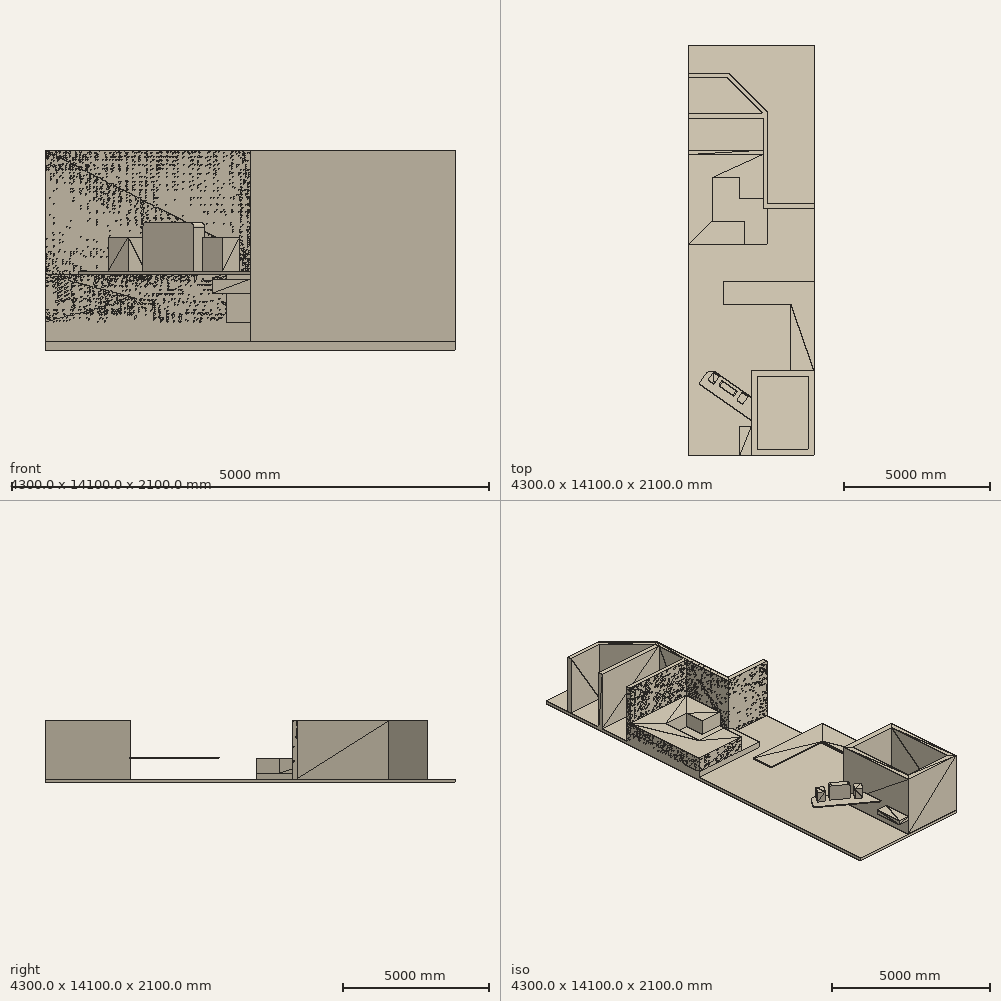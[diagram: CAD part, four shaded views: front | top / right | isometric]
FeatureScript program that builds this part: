
annotation { "Feature Type Name" : "Feature", "Feature Type Description" : "" }
export const myFeature = defineFeature(function(context is Context, id is Id, definition is map)
    precondition{}
    {
        {
            var Q0;
            Q0=qCreatedBy(makeId("Top.planeOp"),FACE);
            var sketch = newSketch(context, id + "F0", { "sketchPlane" : qUnion([Q0])});
            skLineSegment(sketch, "E0.bottom", {"start": v(0, 0) * mm, "end": v(4300, 0) * mm});
            skLineSegment(sketch, "E0.top", {"start": v(0, 14100) * mm, "end": v(4300, 14100) * mm});
            skLineSegment(sketch, "E0.left", {"start": v(0, 0) * mm, "end": v(0, 14100) * mm});
            skLineSegment(sketch, "E0.right", {"start": v(4300, 0) * mm, "end": v(4300, 14100) * mm});
            skLineSegment(sketch, "E1.bottom", {"start": v(-500, -500) * mm, "end": v(4800, -500) * mm});
            skLineSegment(sketch, "E1.top", {"start": v(-500, 14600) * mm, "end": v(4800, 14600) * mm});
            skLineSegment(sketch, "E1.left", {"start": v(-500, -500) * mm, "end": v(-500, 14600) * mm});
            skLineSegment(sketch, "E1.right", {"start": v(4800, -500) * mm, "end": v(4800, 14600) * mm});
            skLineSegment(sketch, "E2", {"start": v(0, 0) * mm, "end": v(-500, -500) * mm});
            skLineSegment(sketch, "E3", {"start": v(4300, 0) * mm, "end": v(4800, -500) * mm});
            skLineSegment(sketch, "E4", {"start": v(-500, 14600) * mm, "end": v(0, 14100) * mm});
            skLineSegment(sketch, "E5", {"start": v(4300, 14100) * mm, "end": v(4800, 14600) * mm});
            skSolve(sketch);
        }
        {
            var Q0;
            Q0=qCreatedBy(makeId("Top.planeOp"),FACE);
            var sketch = newSketch(context, id + "F1", { "sketchPlane" : qUnion([Q0])});
            skLineSegment(sketch, "E6.bottom", {"start": v(2350, 210) * mm, "end": v(4100, 210) * mm});
            skLineSegment(sketch, "E6.top", {"start": v(2350, 2710) * mm, "end": v(4100, 2710) * mm});
            skLineSegment(sketch, "E6.left", {"start": v(2350, 210) * mm, "end": v(2350, 2710) * mm});
            skLineSegment(sketch, "E6.right", {"start": v(4100, 210) * mm, "end": v(4100, 2710) * mm});
            skLineSegment(sketch, "E7.top", {"start": v(2150, 2910) * mm, "end": v(4300, 2910) * mm});
            skLineSegment(sketch, "E7.right", {"start": v(4300, 10) * mm, "end": v(4300, 2910) * mm});
            skLineSegment(sketch, "E8", {"start": v(2150, 2910) * mm, "end": v(2150, 10) * mm});
            skLineSegment(sketch, "E9", {"start": v(2150, 10) * mm, "end": v(4300, 10) * mm});
            skSolve(sketch);
        }
        {
            var Q0;
            Q0=qCreatedBy(makeId("Top.planeOp"),FACE);
            var sketch = newSketch(context, id + "F2", { "sketchPlane" : qUnion([Q0])});
            skLineSegment(sketch, "E10.bottom", {"start": v(346.87, 2461.87) * mm, "end": v(2149, 1200) * mm});
            skLineSegment(sketch, "E10.top", {"start": v(927.53, 2855.28) * mm, "end": v(2149, 2000) * mm});
            skLineSegment(sketch, "E10.right", {"start": v(2149, 1200) * mm, "end": v(2149, 2000) * mm});
            skLineSegment(sketch, "E11.bottom", {"start": v(4300, 2900) * mm, "end": v(3500, 2900) * mm});
            skLineSegment(sketch, "E11.top", {"start": v(4300, 6000) * mm, "end": v(3500, 6000) * mm});
            skLineSegment(sketch, "E11.left", {"start": v(4300, 2900) * mm, "end": v(4300, 6000) * mm});
            skLineSegment(sketch, "E11.right", {"start": v(3500, 2900) * mm, "end": v(3500, 6000) * mm});
            skLineSegment(sketch, "E12.bottom", {"start": v(3500, 6000) * mm, "end": v(1200, 6000) * mm});
            skLineSegment(sketch, "E12.top", {"start": v(3500, 5200) * mm, "end": v(1200, 5200) * mm});
            skLineSegment(sketch, "E12.left", {"start": v(3500, 6000) * mm, "end": v(3500, 5200) * mm});
            skLineSegment(sketch, "E12.right", {"start": v(1200, 6000) * mm, "end": v(1200, 5200) * mm});
            skLineSegment(sketch, "E13", {"start": v(579.35, 2793.89) * mm, "end": v(346.87, 2461.87) * mm});
            skPoint(sketch, "E14.visualSharp", {"position": v(2149, 1200) * mm});
            skPoint(sketch, "E15.visualSharp", {"position": v(722.74, 2998.68) * mm});
            skArc(sketch, "E15.filletArc", {"start": v(927.53, 2855.28) * mm, "mid": v(740.72, 2896.7) * mm, "end": v(579.35, 2793.89) * mm});
            skLineSegment(sketch, "E16.bottom", {"start": v(2149, 1) * mm, "end": v(1749, 1) * mm});
            skLineSegment(sketch, "E16.top", {"start": v(2149, 1001) * mm, "end": v(1749, 1001) * mm});
            skLineSegment(sketch, "E16.left", {"start": v(2149, 1) * mm, "end": v(2149, 1001) * mm});
            skLineSegment(sketch, "E16.right", {"start": v(1749, 1) * mm, "end": v(1749, 1001) * mm});
            skSolve(sketch);
        }
        {
            var Q0;
            Q0=qCreatedBy(makeId("Top.planeOp"),FACE);
            var sketch = newSketch(context, id + "F3", { "sketchPlane" : qUnion([Q0])});
            skLineSegment(sketch, "E17.bottom", {"start": v(0, 7250) * mm, "end": v(2700, 7250) * mm});
            skLineSegment(sketch, "E17.top", {"start": v(0, 10350) * mm, "end": v(2700, 10350) * mm});
            skLineSegment(sketch, "E17.left", {"start": v(0, 7250) * mm, "end": v(0, 10350) * mm});
            skLineSegment(sketch, "E17.right", {"start": v(2700, 7250) * mm, "end": v(2700, 10350) * mm});
            skLineSegment(sketch, "E18.bottom", {"start": v(0, 10350) * mm, "end": v(3100, 10350) * mm});
            skLineSegment(sketch, "E18.top", {"start": v(0, 6850) * mm, "end": v(3100, 6850) * mm});
            skLineSegment(sketch, "E18.left", {"start": v(0, 10350) * mm, "end": v(0, 6850) * mm});
            skLineSegment(sketch, "E18.right", {"start": v(3100, 10350) * mm, "end": v(3100, 6850) * mm});
            skSolve(sketch);
        }
        {
            var Q0;
            Q0=qCreatedBy(makeId("Top.planeOp"),FACE);
            var sketch = newSketch(context, id + "F4", { "sketchPlane" : qUnion([Q0])});
            skLineSegment(sketch, "E19", {"start": v(0, 7250) * mm, "end": v(1900, 7250) * mm});
            skLineSegment(sketch, "E20", {"start": v(1900, 7250) * mm, "end": v(1900, 8050) * mm});
            skLineSegment(sketch, "E21", {"start": v(1900, 8050) * mm, "end": v(800, 8050) * mm});
            skLineSegment(sketch, "E22", {"start": v(800, 8050) * mm, "end": v(800, 9550) * mm});
            skLineSegment(sketch, "E23", {"start": v(800, 9550) * mm, "end": v(1750, 9550) * mm});
            skLineSegment(sketch, "E24", {"start": v(1750, 9550) * mm, "end": v(1750, 8850) * mm});
            skLineSegment(sketch, "E25", {"start": v(1750, 8850) * mm, "end": v(2550, 8850) * mm});
            skLineSegment(sketch, "E26", {"start": v(2550, 8850) * mm, "end": v(2550, 10350) * mm});
            skLineSegment(sketch, "E27", {"start": v(2550, 10350) * mm, "end": v(0, 10350) * mm});
            skLineSegment(sketch, "E28", {"start": v(0, 10350) * mm, "end": v(0, 7250) * mm});
            skSolve(sketch);
        }
        {
            var Q0;
            Q0=qCreatedBy(makeId("Top.planeOp"),FACE);
            var sketch = newSketch(context, id + "F5", { "sketchPlane" : qUnion([Q0])});
            skLineSegment(sketch, "E29", {"start": v(4300, 8500) * mm, "end": v(2550, 8500) * mm});
            skLineSegment(sketch, "E30", {"start": v(2550, 8500) * mm, "end": v(2550, 11750) * mm});
            skLineSegment(sketch, "E31", {"start": v(2550, 11750) * mm, "end": v(1300, 13000) * mm});
            skLineSegment(sketch, "E32", {"start": v(1300, 13000) * mm, "end": v(0, 13000) * mm});
            skLineSegment(sketch, "E33", {"start": v(4300, 8500) * mm, "end": v(4300, 8650) * mm});
            skLineSegment(sketch, "E34", {"start": v(4300, 8650) * mm, "end": v(2700, 8650) * mm});
            skLineSegment(sketch, "E35", {"start": v(2700, 8650) * mm, "end": v(2700, 11812.13) * mm});
            skLineSegment(sketch, "E36", {"start": v(2700, 11812.13) * mm, "end": v(1362.13, 13150) * mm});
            skLineSegment(sketch, "E37", {"start": v(1362.13, 13150) * mm, "end": v(0, 13150) * mm});
            skLineSegment(sketch, "E38", {"start": v(0, 13150) * mm, "end": v(0, 13000) * mm});
            skLineSegment(sketch, "E39.bottom", {"start": v(2550, 10350) * mm, "end": v(0, 10350) * mm});
            skLineSegment(sketch, "E39.top", {"start": v(2550, 10500) * mm, "end": v(0, 10500) * mm});
            skLineSegment(sketch, "E39.left", {"start": v(2550, 10350) * mm, "end": v(2550, 10500) * mm});
            skLineSegment(sketch, "E39.right", {"start": v(0, 10350) * mm, "end": v(0, 10500) * mm});
            skLineSegment(sketch, "E40.bottom", {"start": v(2550, 11750) * mm, "end": v(0, 11750) * mm});
            skLineSegment(sketch, "E40.top", {"start": v(2550, 11600) * mm, "end": v(0, 11600) * mm});
            skLineSegment(sketch, "E40.left", {"start": v(2550, 11750) * mm, "end": v(2550, 11600) * mm});
            skLineSegment(sketch, "E40.right", {"start": v(0, 11750) * mm, "end": v(0, 11600) * mm});
            skSolve(sketch);
        }
        {
            var Q0;
            Q0=makeQuery(id+"F0.imprint","IMPRINT",FACE,{"disambiguationData":[TD([[makeQuery(id+"F0.imprint","IMPRINT",EDGE,{"derivedFrom":sQuery(id+"F0.wireOp",EDGE,"E0.bottom")}),1.0]])]});
            var sketch = newSketch(context, id + "F6", { "sketchPlane" : qUnion([Q0])});
            skLineSegment(sketch, "E41", {"start": v(842.44, 2853.82) * mm, "end": v(657.75, 2590.05) * mm});
            skLineSegment(sketch, "E42", {"start": v(657.75, 2590.05) * mm, "end": v(866.64, 2443.8) * mm});
            skLineSegment(sketch, "E43", {"start": v(866.64, 2443.8) * mm, "end": v(1051.33, 2707.56) * mm});
            skLineSegment(sketch, "E44", {"start": v(1051.33, 2707.56) * mm, "end": v(842.44, 2853.82) * mm});
            skLineSegment(sketch, "E45", {"start": v(1829.52, 2162.66) * mm, "end": v(1644.83, 1898.9) * mm});
            skLineSegment(sketch, "E46", {"start": v(1644.83, 1898.9) * mm, "end": v(1853.71, 1752.63) * mm});
            skLineSegment(sketch, "E47", {"start": v(1853.71, 1752.63) * mm, "end": v(2038.4, 2016.4) * mm});
            skLineSegment(sketch, "E48", {"start": v(2038.4, 2016.4) * mm, "end": v(1829.52, 2162.66) * mm});
            skLineSegment(sketch, "E49", {"start": v(1138.05, 2569.9) * mm, "end": v(1021.61, 2403.6) * mm});
            skLineSegment(sketch, "E50", {"start": v(1021.61, 2403.6) * mm, "end": v(1554.06, 2030.78) * mm});
            skLineSegment(sketch, "E51", {"start": v(1554.06, 2030.78) * mm, "end": v(1670.5, 2197.07) * mm});
            skLineSegment(sketch, "E52", {"start": v(1670.5, 2197.07) * mm, "end": v(1138.05, 2569.9) * mm});
            skPoint(sketch, "E53", {"position": v(1737.18, 2030.78) * mm});
            skSolve(sketch);
        }
        {
            var Q0;
            Q0=makeQuery(id+"F1.imprint","IMPRINT",FACE,{"disambiguationData":[TD([[makeQuery(id+"F1.imprint","IMPRINT",EDGE,{"derivedFrom":sQuery(id+"F1.wireOp",EDGE,"E6.top")}),1.0]])]});
            extrude(context, id + "F7", {"entities" : qUnion([Q0]), "depth" : 2000 * mm});
        }
        {
            var Q0;
            Q0=makeQuery(id+"F2.imprint","IMPRINT",FACE,{"disambiguationData":[TD([[makeQuery(id+"F2.imprint","IMPRINT",EDGE,{"derivedFrom":sQuery(id+"F2.wireOp",EDGE,"E10.bottom")}),1.0]])]});
            var Q1;
            Q1=makeQuery(id+"F2.imprint","IMPRINT",FACE,{"disambiguationData":[TD([[makeQuery(id+"F2.imprint","IMPRINT",EDGE,{"derivedFrom":sQuery(id+"F2.wireOp",EDGE,"E11.bottom")}),-1.0]])]});
            var Q2;
            Q2=makeQuery(id+"F2.imprint","IMPRINT",FACE,{"disambiguationData":[TD([[makeQuery(id+"F2.imprint","IMPRINT",EDGE,{"derivedFrom":sQuery(id+"F2.wireOp",EDGE,"E12.bottom")}),1.0]])]});
            extrude(context, id + "F8", {"entities" : qUnion([Q0, Q1, Q2]), "depth" : 730 * mm, "hasSecondDirection" : true, "secondDirectionOppositeDirection" : false, "secondDirectionDepth" : 700 * mm});
        }
        {
            var Q0;
            Q0=makeQuery(id+"F0.imprint","IMPRINT",FACE,{"disambiguationData":[TD([[makeQuery(id+"F0.imprint","IMPRINT",EDGE,{"derivedFrom":sQuery(id+"F0.wireOp",EDGE,"E0.bottom")}),1.0]])]});
            extrude(context, id + "F9", {"entities" : qUnion([Q0]), "oppositeDirection" : true, "depth" : 100 * mm});
        }
        {
            var Q0;
            {var subQ0=sQuery(id+"F3.wireOp",EDGE,"E17.bottom");Q0=makeQuery(id+"F3.imprint","IMPRINT",FACE,{"disambiguationData":[TD([[makeQuery(id+"F3.imprint","IMPRINT",EDGE,{"derivedFrom":subQ0}),1.0]])]});}
            extrude(context, id + "F10", {"entities" : qUnion([Q0]), "operationType" : NewBodyOperationType.ADD, "depth" : 200 * mm});
        }
        {
            var Q0;
            Q0=makeQuery(id+"F4.imprint","IMPRINT",FACE,{"disambiguationData":[TD([[makeQuery(id+"F4.imprint","IMPRINT",EDGE,{"derivedFrom":sQuery(id+"F4.wireOp",EDGE,"E19")}),1.0]])]});
            extrude(context, id + "F11", {"entities" : qUnion([Q0]), "depth" : 700 * mm, "hasSecondDirection" : true, "secondDirectionOppositeDirection" : false, "secondDirectionDepth" : 200 * mm});
        }
        {
            var Q0;
            Q0 = qSketchRegion(id + "F5", true);
            extrude(context, id + "F12", {"entities" : qUnion([Q0]), "depth" : 2000 * mm});
        }
        {
            var Q0;
            Q0=makeQuery(id+"F2.imprint","IMPRINT",FACE,{"disambiguationData":[TD([[makeQuery(id+"F2.imprint","IMPRINT",EDGE,{"derivedFrom":sQuery(id+"F2.wireOp",EDGE,"E16.bottom")}),-1.0]])]});
            extrude(context, id + "F13", {"entities" : qUnion([Q0]), "depth" : 650 * mm, "hasSecondDirection" : true, "secondDirectionOppositeDirection" : false, "secondDirectionDepth" : 500 * mm});
        }
        {
            var Q0;
            Q0=makeQuery(id+"F6.imprint","IMPRINT",FACE,{"disambiguationData":[TD([[makeQuery(id+"F6.imprint","IMPRINT",EDGE,{"derivedFrom":sQuery(id+"F6.wireOp",EDGE,"E41")}),1.0]])]});
            var Q1;
            Q1=makeQuery(id+"F6.imprint","IMPRINT",FACE,{"disambiguationData":[TD([[makeQuery(id+"F6.imprint","IMPRINT",EDGE,{"derivedFrom":sQuery(id+"F6.wireOp",EDGE,"E45")}),1.0]])]});
            extrude(context, id + "F14", {"entities" : qUnion([Q0, Q1]), "depth" : 1088 * mm, "hasSecondDirection" : true, "secondDirectionOppositeDirection" : false, "secondDirectionDepth" : 730 * mm});
        }
        {
            var Q0;
            Q0=makeQuery(id+"F6.imprint","IMPRINT",FACE,{"disambiguationData":[TD([[makeQuery(id+"F6.imprint","IMPRINT",EDGE,{"derivedFrom":sQuery(id+"F6.wireOp",EDGE,"E49")}),1.0]])]});
            var Q1;
            Q1=makeQuery(id+"F8.opExtrude","SWEPT_BODY",BODY,{"disambiguationData":[OSD([sQuery(id+"F2.wireOp",EDGE,"E10.bottom"),sQuery(id+"F2.wireOp",EDGE,"E10.top"),sQuery(id+"F2.wireOp",EDGE,"E10.right"),sQuery(id+"F2.wireOp",EDGE,"E13"),sQuery(id+"F2.wireOp",EDGE,"E15.filletArc")])]});
            extrude(context, id + "F15", {"entities" : qUnion([Q0]), "operationType" : NewBodyOperationType.ADD, "endBoundEntityBody" : qUnion([Q1]), "depth" : 1246 * mm, "hasSecondDirection" : true, "secondDirectionOppositeDirection" : false, "secondDirectionDepth" : 730 * mm});
        }
        {
            var Q0;
            Q0=makeQuery(id+"F15.opExtrude","CAP_EDGE",EDGE,{"disambiguationData":[OSD([sQuery(id+"F6.wireOp",EDGE,"E49")])],"isStart":false});
            var Q1;
            Q1=makeQuery(id+"F15.opExtrude","CAP_EDGE",EDGE,{"disambiguationData":[OSD([sQuery(id+"F6.wireOp",EDGE,"E51")])],"isStart":false});
            fillet(context, id + "F16", {"entities" : qUnion([Q0, Q1]), "radius" : 50 * mm, "tangentPropagation" : true, "allowEdgeOverflow" : false});
        }
    });
